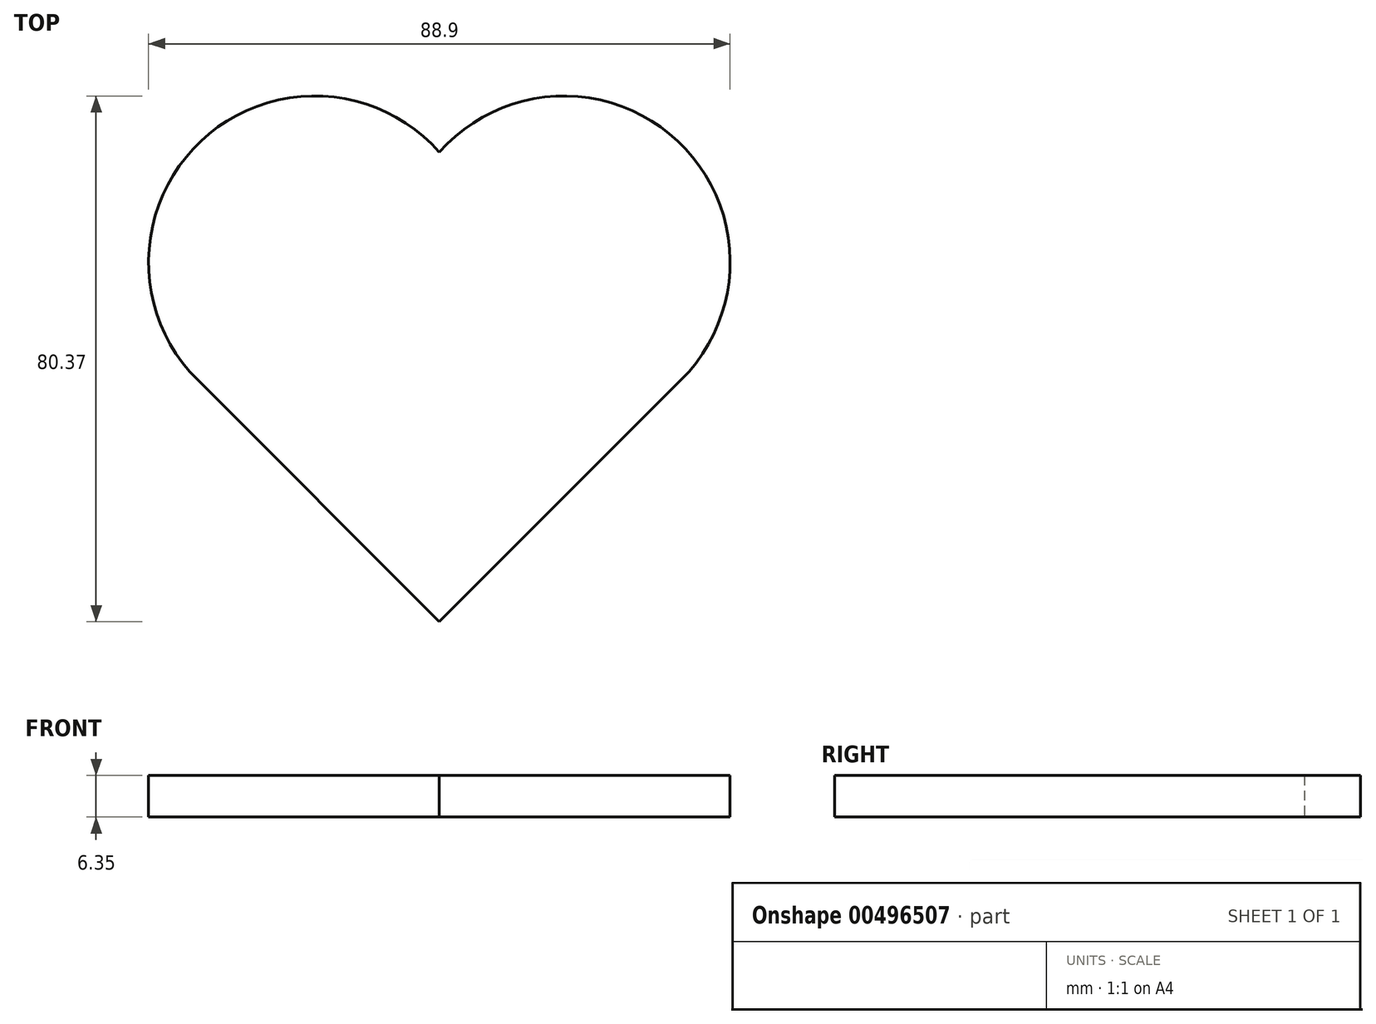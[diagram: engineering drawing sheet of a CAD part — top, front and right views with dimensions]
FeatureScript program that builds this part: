
annotation { "Feature Type Name" : "Feature", "Feature Type Description" : "" }
export const myFeature = defineFeature(function(context is Context, id is Id, definition is map)
    precondition{}
    {
        {
            var Q0;
            Q0=qCreatedBy(makeId("Top.planeOp"),FACE);
            var sketch = newSketch(context, id + "F0", { "sketchPlane" : qUnion([Q0])});
            skCircle(sketch, "E0", {"center": v(0, 0) * mm, "radius": 25.4 * mm});
            skCircle(sketch, "E1", {"center": v(38.1, 0) * mm, "radius": 25.4 * mm});
            skLineSegment(sketch, "E2", {"start": v(0, 0) * mm, "end": v(-41.5, -41.5) * mm, "construction": true});
            skLineSegment(sketch, "E3", {"start": v(-63.6, 0) * mm, "end": v(76.1, 0) * mm, "construction": true});
            skLineSegment(sketch, "E4", {"start": v(19.05, -16.8) * mm, "end": v(19.05, -93.14) * mm, "construction": true});
            skLineSegment(sketch, "E5", {"start": v(-17.96, -17.96) * mm, "end": v(19.05, -54.97) * mm});
            skLineSegment(sketch, "E6", {"start": v(19.05, -54.97) * mm, "end": v(56.06, -17.96) * mm});
            skLineSegment(sketch, "E7", {"start": v(-36.46, -17.96) * mm, "end": v(68.71, -17.96) * mm, "construction": true});
            skSolve(sketch);
        }
        {
            var Q0;
            Q0 = qSketchRegion(id + "F0", true);
            extrude(context, id + "F1", {"entities" : qUnion([Q0]), "depth" : 6.35 * mm});
        }
    });
